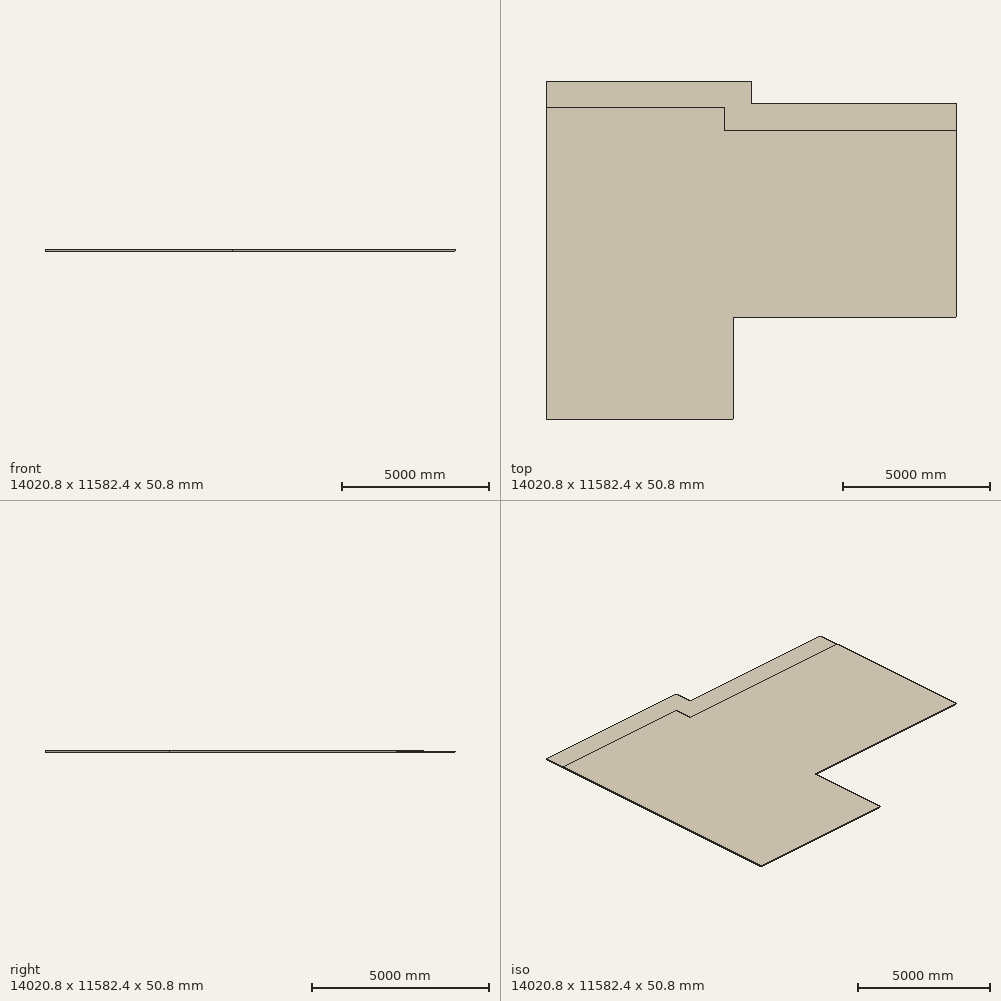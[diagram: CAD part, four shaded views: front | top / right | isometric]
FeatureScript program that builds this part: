
annotation { "Feature Type Name" : "Feature", "Feature Type Description" : "" }
export const myFeature = defineFeature(function(context is Context, id is Id, definition is map)
    precondition{}
    {
        {
            var Q0;
            Q0=qCreatedBy(makeId("Top.planeOp"),FACE);
            var sketch = newSketch(context, id + "F0", { "sketchPlane" : qUnion([Q0])});
            skLineSegment(sketch, "E0", {"start": v(0, 0) * mm, "end": v(0, 11582.4) * mm});
            skLineSegment(sketch, "E1", {"start": v(0, 0) * mm, "end": v(6400.8, 0) * mm});
            skLineSegment(sketch, "E2", {"start": v(6400.8, 0) * mm, "end": v(6400.8, 3505.2) * mm});
            skLineSegment(sketch, "E3", {"start": v(6400.8, 3505.2) * mm, "end": v(14020.8, 3505.2) * mm});
            skLineSegment(sketch, "E4", {"start": v(14020.8, 3505.2) * mm, "end": v(14020.8, 10820.4) * mm});
            skLineSegment(sketch, "E5", {"start": v(14020.8, 10820.4) * mm, "end": v(7010.4, 10820.4) * mm});
            skLineSegment(sketch, "E6", {"start": v(7010.4, 10820.4) * mm, "end": v(7010.4, 11582.4) * mm});
            skLineSegment(sketch, "E7", {"start": v(7010.4, 11582.4) * mm, "end": v(0, 11582.4) * mm});
            skSolve(sketch);
        }
        {
            var Q0;
            Q0 = qSketchRegion(id + "F0", true);
            extrude(context, id + "F1", {"entities" : qUnion([Q0]), "depth" : 50.8 * mm, "offsetDistance" : 25.4 * mm});
        }
        {
            var Q0;
            Q0=makeQuery(id+"F1.opExtrude","CAP_FACE",FACE,{"disambiguationData":[OSD([sQuery(id+"F0.wireOp",EDGE,"E0"),sQuery(id+"F0.wireOp",EDGE,"E1"),sQuery(id+"F0.wireOp",EDGE,"E2"),sQuery(id+"F0.wireOp",EDGE,"E3"),sQuery(id+"F0.wireOp",EDGE,"E4"),sQuery(id+"F0.wireOp",EDGE,"pEncvGaK-EmXm-eR2I-vIeD-qa8nqv12E7qZ")])],"isStart":false});
            var sketch = newSketch(context, id + "F2", { "sketchPlane" : qUnion([Q0])});
            skLineSegment(sketch, "E8", {"start": v(0, 10668) * mm, "end": v(6096, 10668) * mm});
            skLineSegment(sketch, "E9", {"start": v(6096, 10668) * mm, "end": v(6096, 9906) * mm});
            skLineSegment(sketch, "E10", {"start": v(6096, 9906) * mm, "end": v(14020.8, 9906) * mm});
            skSolve(sketch);
        }
        {
            var Q0;
            Q0 = qSketchRegion(id + "F2", true);
            var Q1;
            {var subQ3=sQuery(id+"F2.wireOp",EDGE,"E8");Q1=makeQuery(id+"F2.imprint","IMPRINT",FACE,{"disambiguationData":[TD([[makeQuery(id+"F2.imprint","IMPRINT",EDGE,{"derivedFrom":subQ3}),1.0]])]});}
            extrude(context, id + "F3", {"entities" : qUnion([Q0, Q1]), "operationType" : NewBodyOperationType.REMOVE, "oppositeDirection" : true, "depth" : 25.4 * mm, "offsetDistance" : 25.4 * mm});
        }
    });
